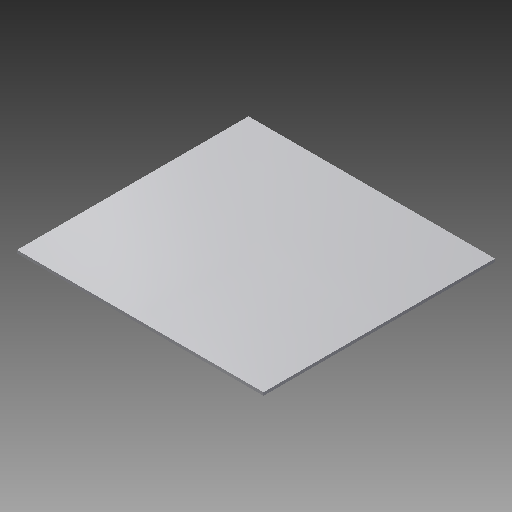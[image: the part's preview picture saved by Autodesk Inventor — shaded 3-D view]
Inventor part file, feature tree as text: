
AUTODESK INVENTOR PART (.ipt)
format: ipt  version: 2018 (Build 220112000, 112)  size: 99,328 bytes
history: native  units: mm
features: extrude x1
ambient origin geometry x8: Origin, YZ Plane, XZ Plane, XY Plane, X Axis, Y Axis, Z Axis, Center Point
bodies: Volumenkörper1 (feature_tree)
feature tree (1):
  extrude  "Extrusion1"  Depth=660.0mm
